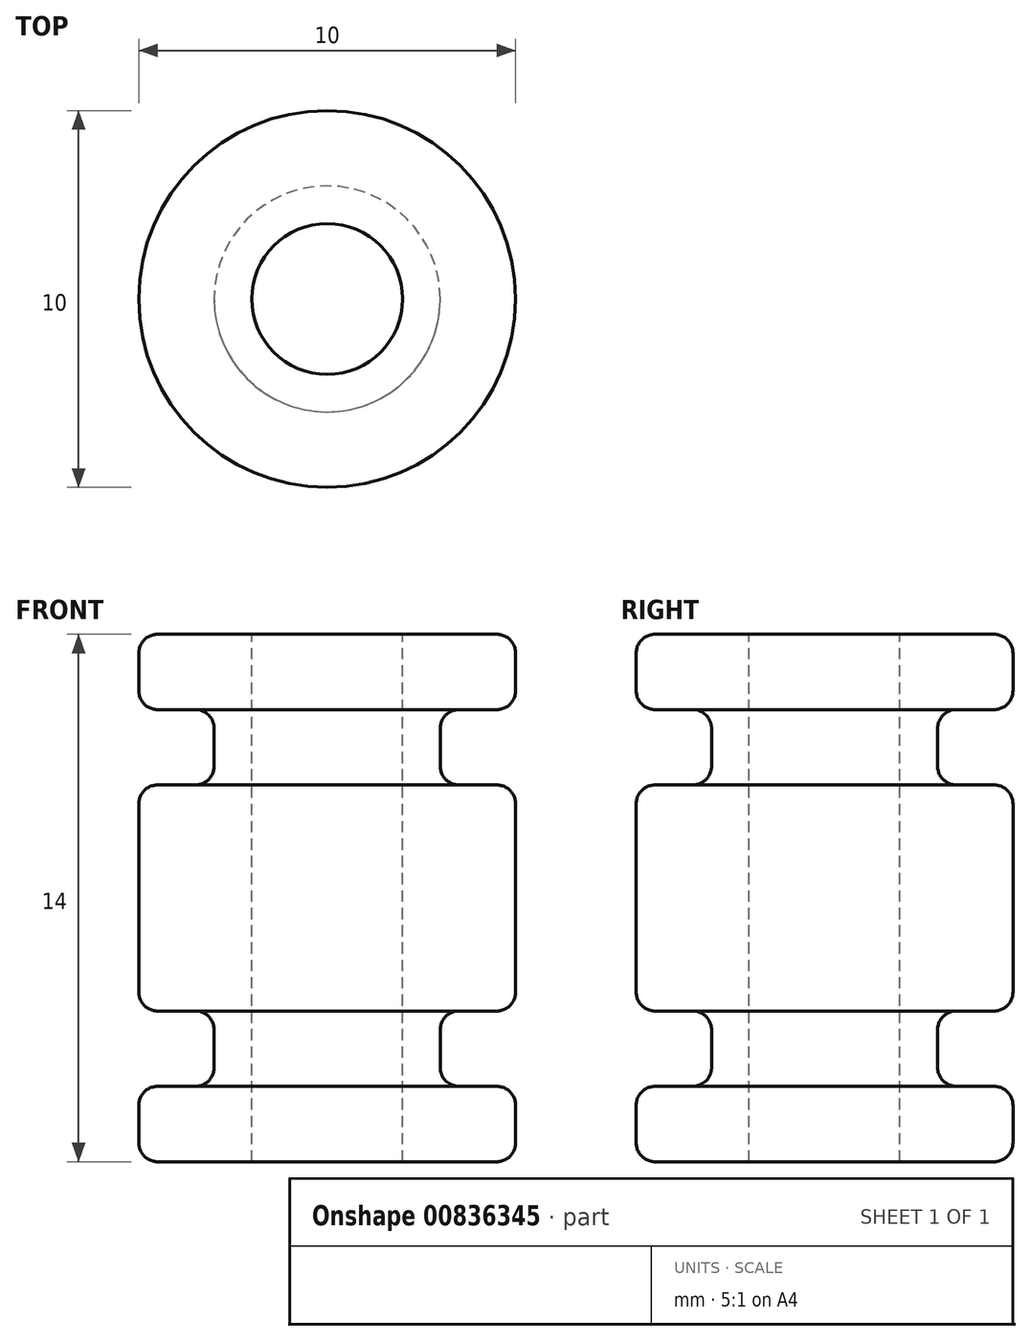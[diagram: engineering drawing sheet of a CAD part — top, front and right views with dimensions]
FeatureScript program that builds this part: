
annotation { "Feature Type Name" : "Feature", "Feature Type Description" : "" }
export const myFeature = defineFeature(function(context is Context, id is Id, definition is map)
    precondition{}
    {
        {
            var Q0;
            Q0=qCreatedBy(makeId("Front.planeOp"),FACE);
            var sketch = newSketch(context, id + "F0", { "sketchPlane" : qUnion([Q0])});
            skLineSegment(sketch, "E0", {"start": v(0, 7) * mm, "end": v(-5, 7) * mm});
            skLineSegment(sketch, "E1", {"start": v(-5, 7) * mm, "end": v(-5, 5) * mm});
            skLineSegment(sketch, "E2", {"start": v(-5, 5) * mm, "end": v(-3, 5) * mm});
            skLineSegment(sketch, "E3", {"start": v(-3, 5) * mm, "end": v(-3, 3) * mm});
            skLineSegment(sketch, "E4", {"start": v(-3, 3) * mm, "end": v(-5, 3) * mm});
            skLineSegment(sketch, "E5", {"start": v(-5, 3) * mm, "end": v(-5, -3) * mm});
            skLineSegment(sketch, "E6", {"start": v(-5, -3) * mm, "end": v(-3, -3) * mm});
            skLineSegment(sketch, "E7", {"start": v(-3, -3) * mm, "end": v(-3, -5) * mm});
            skLineSegment(sketch, "E8", {"start": v(-3, -5) * mm, "end": v(-5, -5) * mm});
            skLineSegment(sketch, "E9", {"start": v(-5, -5) * mm, "end": v(-5, -7) * mm});
            skLineSegment(sketch, "E10", {"start": v(-5, -7) * mm, "end": v(0, -7) * mm});
            skLineSegment(sketch, "E11", {"start": v(0, -7) * mm, "end": v(0, 7) * mm});
            skSolve(sketch);
        }
        {
            var Q0;
            Q0=makeQuery(id+"F0.imprint","IMPRINT",FACE,{"disambiguationData":[TD([[makeQuery(id+"F0.imprint","IMPRINT",EDGE,{"derivedFrom":sQuery(id+"F0.wireOp",EDGE,"E0")}),1.0]])]});
            var Q1;
            Q1=sQuery(id+"F0.wireOp",EDGE,"E11");
            revolve(context, id + "F1", {"surfaceOperationType" : NewSurfaceOperationType.NEW, "entities" : qUnion([Q0]), "axis" : qUnion([Q1]), "revolveType" : RevolveType.FULL});
        }
        {
            var Q0;
            Q0=qCreatedBy(makeId("Top.planeOp"),FACE);
            var sketch = newSketch(context, id + "F2", { "sketchPlane" : qUnion([Q0])});
            skCircle(sketch, "E12", {"center": v(0, 0) * mm, "radius": 2 * mm});
            skSolve(sketch);
        }
        {
            var Q0;
            Q0=qSketchRegion(id+"F2",true);
            extrude(context, id + "F3", {"entities" : qUnion([Q0]), "operationType" : NewBodyOperationType.REMOVE, "endBound" : BoundingType.SYMMETRIC, "oppositeDirection" : true, "depth" : 100 * mm, "offsetDistance" : 25 * mm});
        }
        {
            var Q0;
            Q0=makeQuery(id+"F1.opRevolve","SWEPT_FACE",FACE,{"disambiguationData":[OSD([sQuery(id+"F0.wireOp",EDGE,"E1")])]});
            var Q1;
            Q1=makeQuery(id+"F1.opRevolve","SWEPT_FACE",FACE,{"disambiguationData":[OSD([sQuery(id+"F0.wireOp",EDGE,"E5")])]});
            var Q2;
            Q2=makeQuery(id+"F1.opRevolve","SWEPT_FACE",FACE,{"disambiguationData":[OSD([sQuery(id+"F0.wireOp",EDGE,"E9")])]});
            var Q3;
            Q3=makeQuery(id+"F1.opRevolve","SWEPT_FACE",FACE,{"disambiguationData":[OSD([sQuery(id+"F0.wireOp",EDGE,"E7")])]});
            var Q4;
            Q4=makeQuery(id+"F1.opRevolve","SWEPT_FACE",FACE,{"disambiguationData":[OSD([sQuery(id+"F0.wireOp",EDGE,"E3")])]});
            fillet(context, id + "F4", {"entities" : qUnion([Q0, Q1, Q2, Q3, Q4]), "radius" : 0.5 * mm, "tangentPropagation" : true, "allowEdgeOverflow" : false});
        }
    });
